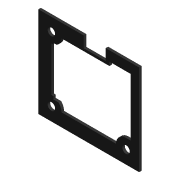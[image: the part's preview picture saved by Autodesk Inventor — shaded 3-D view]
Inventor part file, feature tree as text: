
AUTODESK INVENTOR PART (.ipt)
format: ipt  version: 2015 SP1 (Build 190203100, 203)  size: 186,880 bytes
history: native  units: mm
features: extrude x3, other x1, sketch x1
ambient origin geometry x8: Origin, YZ Plane, XZ Plane, XY Plane, X Axis, Y Axis, Z Axis, Center Point
bodies: Body1 (feature_tree)
feature tree (5):
  other  "Твердое тело1"
  extrude  "Выдавливание1"  Depth=1.0mm TaperAngle=0.0deg
  extrude  "Выдавливание2"  Depth=1.0mm TaperAngle=0.0deg
  extrude  "Выдавливание3"  Depth=1.0mm TaperAngle=0.0deg
  sketch  "Эскиз1"
